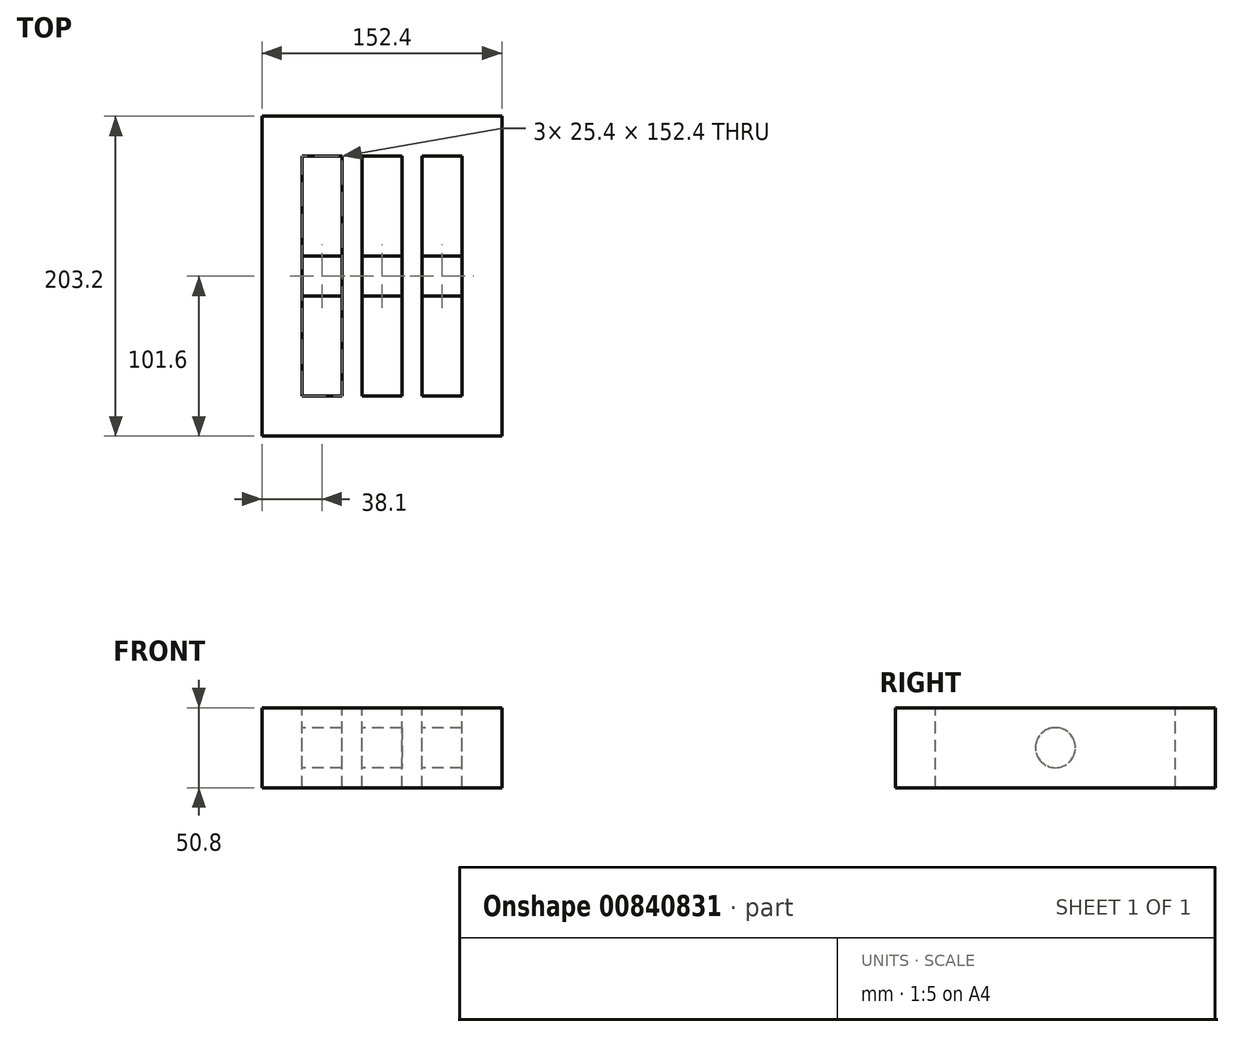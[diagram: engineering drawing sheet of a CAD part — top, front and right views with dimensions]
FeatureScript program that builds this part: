
annotation { "Feature Type Name" : "Feature", "Feature Type Description" : "" }
export const myFeature = defineFeature(function(context is Context, id is Id, definition is map)
    precondition{}
    {
        {
            var Q0;
            Q0=qCreatedBy(makeId("Top.planeOp"),FACE);
            var sketch = newSketch(context, id + "F0", { "sketchPlane" : qUnion([Q0])});
            skLineSegment(sketch, "E0.bottom", {"start": v(-101.6, 177.8) * mm, "end": v(50.8, 177.8) * mm});
            skLineSegment(sketch, "E0.right", {"start": v(50.8, 177.8) * mm, "end": v(50.8, -127) * mm});
            skLineSegment(sketch, "E1.left", {"start": v(-101.6, 177.8) * mm, "end": v(-101.6, 152.4) * mm});
            skLineSegment(sketch, "E1.right", {"start": v(50.8, 177.8) * mm, "end": v(50.8, 127) * mm});
            skLineSegment(sketch, "E2.bottom", {"start": v(-50.8, 0) * mm, "end": v(-76.2, 0) * mm});
            skLineSegment(sketch, "E2.top", {"start": v(-50.8, 152.4) * mm, "end": v(-76.2, 152.4) * mm});
            skLineSegment(sketch, "E2.left", {"start": v(-50.8, 0) * mm, "end": v(-50.8, 152.4) * mm});
            skLineSegment(sketch, "E2.right", {"start": v(-76.2, 0) * mm, "end": v(-76.2, 152.4) * mm});
            skLineSegment(sketch, "E3.bottom", {"start": v(0, 0) * mm, "end": v(25.4, 0) * mm});
            skLineSegment(sketch, "E3.top", {"start": v(0, 152.4) * mm, "end": v(25.4, 152.4) * mm});
            skLineSegment(sketch, "E3.left", {"start": v(0, 0) * mm, "end": v(0, 152.4) * mm});
            skLineSegment(sketch, "E3.right", {"start": v(25.4, 0) * mm, "end": v(25.4, 152.4) * mm});
            skLineSegment(sketch, "E4", {"start": v(-38.1, 0) * mm, "end": v(-38.1, 152.4) * mm});
            skLineSegment(sketch, "E5", {"start": v(-38.1, 152.4) * mm, "end": v(-12.7, 152.4) * mm});
            skLineSegment(sketch, "E6", {"start": v(-12.7, 152.4) * mm, "end": v(-12.7, 0) * mm});
            skLineSegment(sketch, "E7", {"start": v(-12.7, 0) * mm, "end": v(-38.1, 0) * mm});
            skLineSegment(sketch, "E8.bottom", {"start": v(-101.6, 0) * mm, "end": v(50.8, 0) * mm});
            skLineSegment(sketch, "E8.top", {"start": v(-101.6, -25.4) * mm, "end": v(50.8, -25.4) * mm});
            skLineSegment(sketch, "E8.left", {"start": v(-101.6, 0) * mm, "end": v(-101.6, -25.4) * mm});
            skLineSegment(sketch, "E8.right", {"start": v(50.8, 0) * mm, "end": v(50.8, -25.4) * mm});
            skLineSegment(sketch, "E9", {"start": v(-101.6, 152.4) * mm, "end": v(-101.6, 0) * mm});
            skSolve(sketch);
        }
        {
            var Q0;
            Q0=makeQuery(id+"F0.imprint","IMPRINT",FACE,{"disambiguationData":[TD([[makeQuery(id+"F0.imprint","IMPRINT",EDGE,{"derivedFrom":sQuery(id+"F0.wireOp",EDGE,"E0.right")}),-1.0]])]});
            var Q1;
            Q1=makeQuery(id+"F0.imprint","IMPRINT",FACE,{"disambiguationData":[TD([[makeQuery(id+"F0.imprint","IMPRINT",EDGE,{"derivedFrom":sQuery(id+"F0.wireOp",EDGE,"E8.top")}),1.0]])]});
            extrude(context, id + "F1", {"entities" : qUnion([Q0, Q1]), "oppositeDirection" : true, "depth" : 50.8 * mm, "offsetDistance" : 25.4 * mm});
        }
        {
            var Q0;
            Q0=makeQuery(id+"F1.opExtrude","SWEPT_FACE",FACE,{"disambiguationData":[OSD([sQuery(id+"F0.wireOp",EDGE,"E2.right")])]});
            var sketch = newSketch(context, id + "F2", { "sketchPlane" : qUnion([Q0])});
            skLineSegment(sketch, "E10", {"start": v(152.4, 0) * mm, "end": v(152.4, -25.4) * mm});
            skLineSegment(sketch, "E11", {"start": v(150.6, -25.4) * mm, "end": v(152.4, -25.4) * mm});
            skLineSegment(sketch, "E12", {"start": v(76.2, -25.4) * mm, "end": v(152.4, -25.4) * mm});
            skCircle(sketch, "E13", {"center": v(76.2, -25.4) * mm, "radius": 12.7 * mm});
            skSolve(sketch);
        }
        {
            var Q0;
            Q0 = qSketchRegion(id + "F2", true);
            extrude(context, id + "F3", {"entities" : qUnion([Q0]), "operationType" : NewBodyOperationType.ADD, "depth" : 127 * mm, "offsetDistance" : 25.4 * mm});
        }
    });
